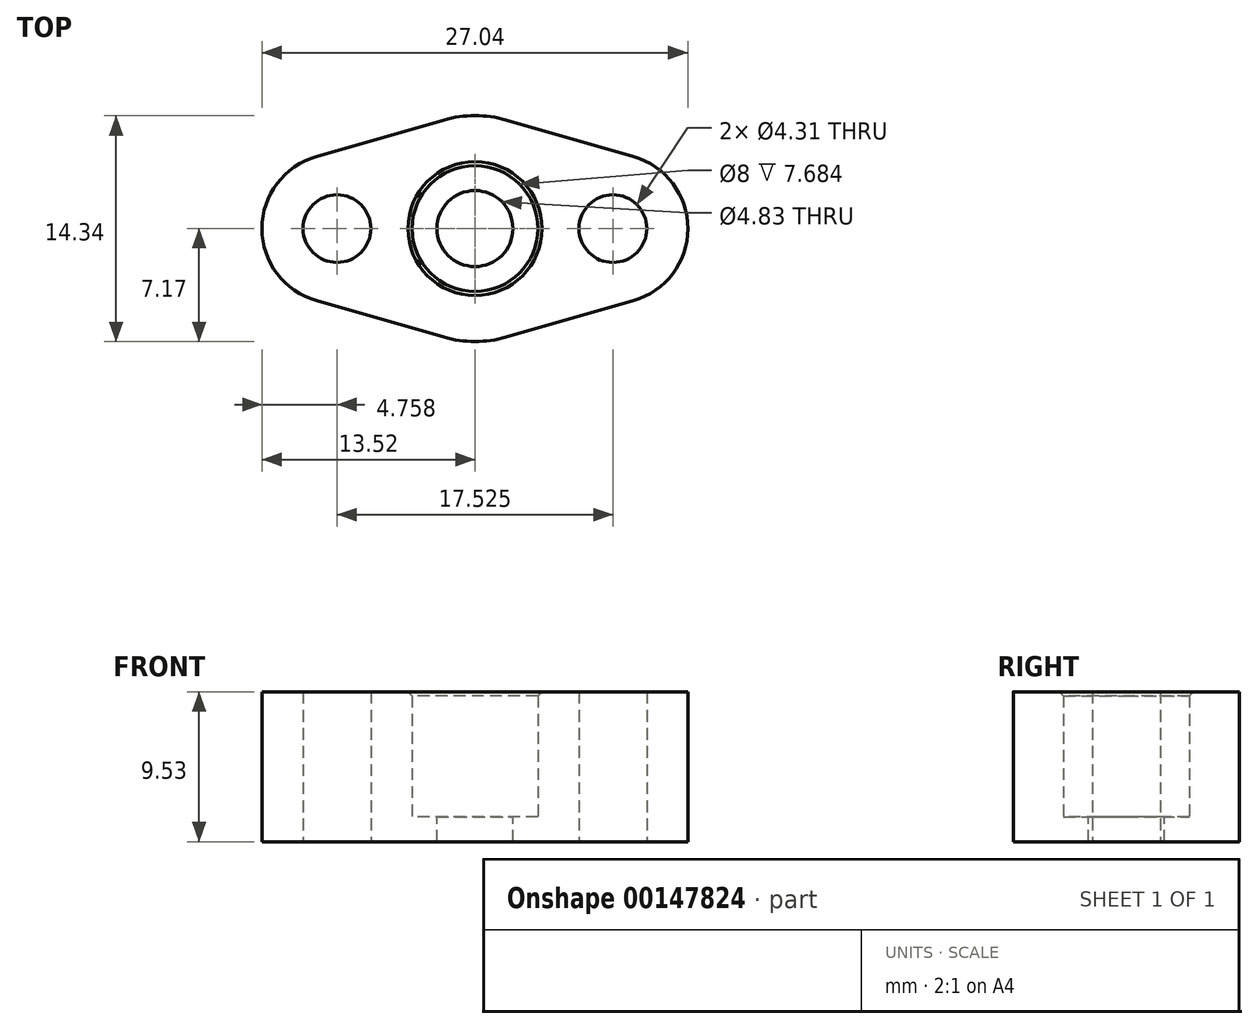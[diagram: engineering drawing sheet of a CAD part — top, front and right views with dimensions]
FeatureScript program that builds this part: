
annotation { "Feature Type Name" : "Feature", "Feature Type Description" : "" }
export const myFeature = defineFeature(function(context is Context, id is Id, definition is map)
    precondition{}
    {
        {
            var Q0;
            Q0=qCreatedBy(makeId("Top.planeOp"),FACE);
            var sketch = newSketch(context, id + "F0", { "sketchPlane" : qUnion([Q0])});
            skCircle(sketch, "E0", {"center": v(0, 0) * mm, "radius": 4 * mm});
            skLineSegment(sketch, "E1", {"start": v(-8.76, 0) * mm, "end": v(8.76, 0) * mm, "construction": true});
            skCircle(sketch, "E2", {"center": v(-8.76, 0) * mm, "radius": 2.15 * mm});
            skCircle(sketch, "E3", {"center": v(8.76, 0) * mm, "radius": 2.15 * mm});
            skArc(sketch, "E4", {"start": v(1.98, 6.9) * mm, "mid": v(0, 7.18) * mm, "end": v(-1.98, 6.9) * mm});
            skArc(sketch, "E5", {"start": v(-10.07, 4.58) * mm, "mid": v(-13.52, 0) * mm, "end": v(-10.07, -4.58) * mm});
            skLineSegment(sketch, "E6", {"start": v(-10.07, 4.58) * mm, "end": v(-1.98, 6.9) * mm});
            skArc(sketch, "E7", {"start": v(-1.98, -6.9) * mm, "mid": v(0, -7.18) * mm, "end": v(1.98, -6.9) * mm});
            skArc(sketch, "E8", {"start": v(10.07, -4.58) * mm, "mid": v(13.52, 0) * mm, "end": v(10.07, 4.58) * mm});
            skLineSegment(sketch, "E9", {"start": v(-10.07, -4.58) * mm, "end": v(-1.98, -6.9) * mm});
            skLineSegment(sketch, "E10", {"start": v(1.98, 6.9) * mm, "end": v(10.07, 4.58) * mm});
            skLineSegment(sketch, "E11", {"start": v(1.98, -6.9) * mm, "end": v(10.07, -4.58) * mm});
            skSolve(sketch);
        }
        {
            var Q0;
            Q0=qSketchRegion(id+"F0",true);
            extrude(context, id + "F1", {"entities" : qUnion([Q0]), "depth" : 7.94 * mm});
        }
        {
            var Q0;
            Q0=makeQuery(id+"F1.opExtrude","CAP_EDGE",EDGE,{"disambiguationData":[OSD([sQuery(id+"F0.wireOp",EDGE,"E0")])],"isStart":false});
            chamfer(context, id + "F2", {"entities" : qUnion([Q0]), "width" : 0.25 * mm});
        }
        {
            var Q0;
            Q0=makeQuery(id+"F1.opExtrude","CAP_FACE",FACE,{"disambiguationData":[OSD([sQuery(id+"F0.wireOp",EDGE,"E0"),sQuery(id+"F0.wireOp",EDGE,"E2"),sQuery(id+"F0.wireOp",EDGE,"E3"),sQuery(id+"F0.wireOp",EDGE,"E4"),sQuery(id+"F0.wireOp",EDGE,"E5"),sQuery(id+"F0.wireOp",EDGE,"E6"),sQuery(id+"F0.wireOp",EDGE,"E7"),sQuery(id+"F0.wireOp",EDGE,"E8"),sQuery(id+"F0.wireOp",EDGE,"E9"),sQuery(id+"F0.wireOp",EDGE,"E10"),sQuery(id+"F0.wireOp",EDGE,"E11")])],"isStart":true});
            var sketch = newSketch(context, id + "F3", { "sketchPlane" : qUnion([Q0])});
            skCircle(sketch, "E12", {"center": v(0, 0) * mm, "radius": 2.41 * mm});
            skSolve(sketch);
        }
        {
            var Q0;
            Q0=makeQuery(id+"F3.imprint","IMPRINT",FACE,{"disambiguationData":[TD([[makeQuery(id+"F3.imprint","IMPRINT",EDGE,{"derivedFrom":makeQuery(id+"F1.opExtrude","CAP_EDGE",EDGE,{"disambiguationData":[OSD([sQuery(id+"F0.wireOp",EDGE,"E0")])],"isStart":true})}),1.0]])]});
            var Q1;
            Q1=makeQuery(id+"F3.imprint","IMPRINT",FACE,{"disambiguationData":[TD([[makeQuery(id+"F3.imprint","IMPRINT",EDGE,{"derivedFrom":sQuery(id+"F3.wireOp",EDGE,"E12")}),-1.0]])]});
            extrude(context, id + "F4", {"entities" : qUnion([Q0, Q1]), "operationType" : NewBodyOperationType.ADD, "depth" : 1.59 * mm});
        }
    });
